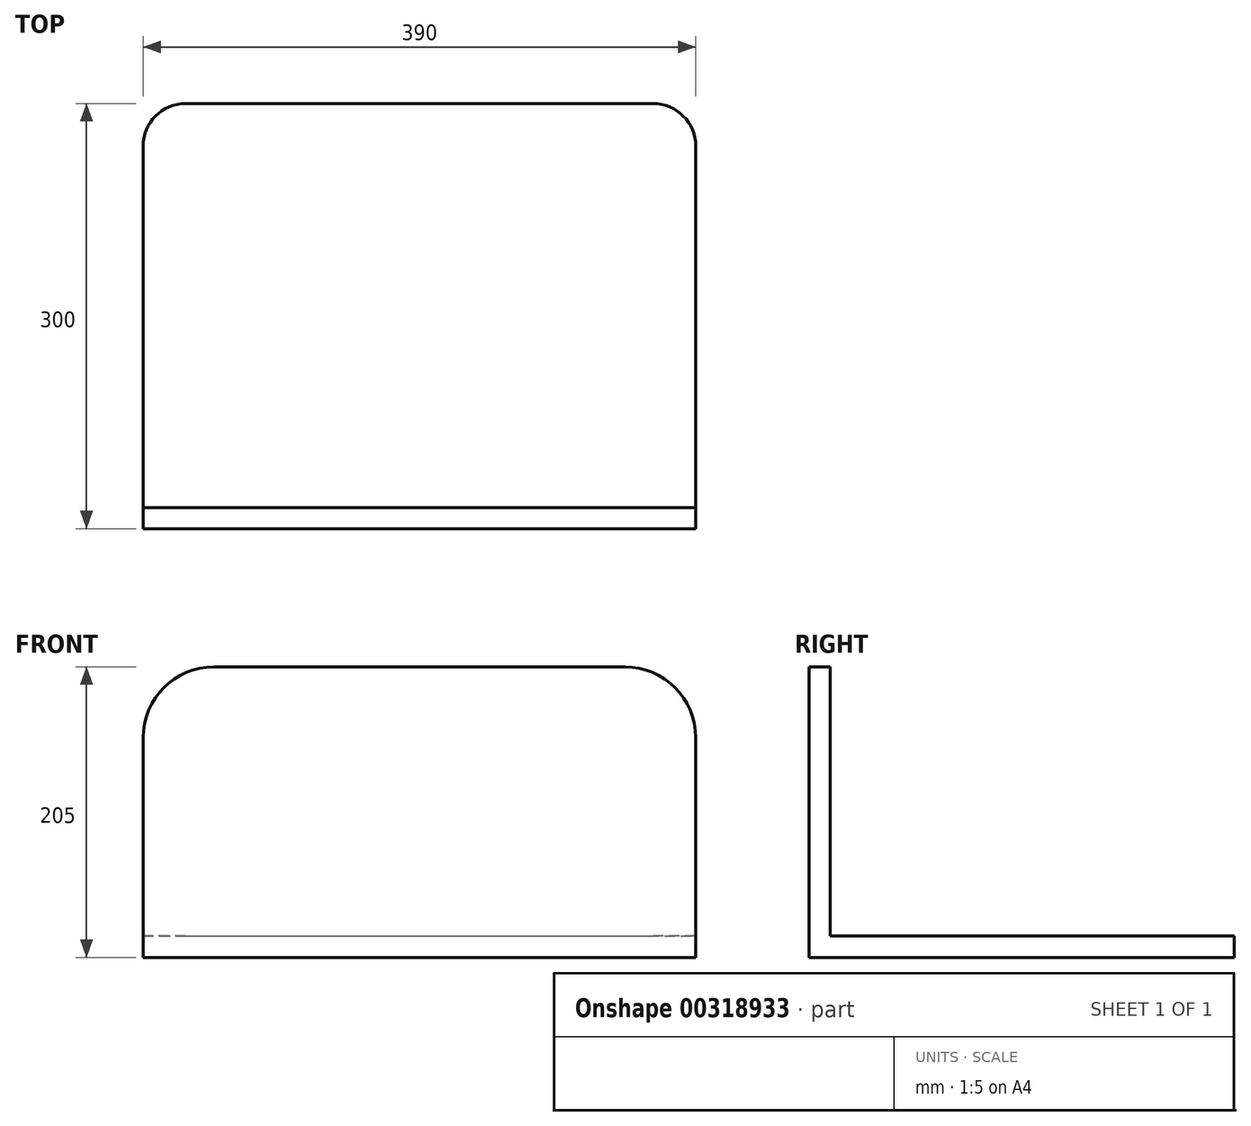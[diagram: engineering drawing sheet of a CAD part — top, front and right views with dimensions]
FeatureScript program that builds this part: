
annotation { "Feature Type Name" : "Feature", "Feature Type Description" : "" }
export const myFeature = defineFeature(function(context is Context, id is Id, definition is map)
    precondition{}
    {
        {
            var Q0;
            Q0=qCreatedBy(makeId("Top.planeOp"),FACE);
            var sketch = newSketch(context, id + "F0", { "sketchPlane" : qUnion([Q0])});
            skLineSegment(sketch, "E0.bottom", {"start": v(-195, -150) * mm, "end": v(195, -150) * mm});
            skLineSegment(sketch, "E0.top", {"start": v(-165, 150) * mm, "end": v(165, 150) * mm});
            skLineSegment(sketch, "E0.left", {"start": v(-195, -150) * mm, "end": v(-195, 120) * mm});
            skLineSegment(sketch, "E0.right", {"start": v(195, -150) * mm, "end": v(195, 120) * mm});
            skPoint(sketch, "E1.visualSharp", {"position": v(-195, 150) * mm});
            skArc(sketch, "E1.filletArc", {"start": v(-165, 150) * mm, "mid": v(-186.21, 141.21) * mm, "end": v(-195, 120) * mm});
            skPoint(sketch, "E2.visualSharp", {"position": v(195, 150) * mm});
            skArc(sketch, "E2.filletArc", {"start": v(195, 120) * mm, "mid": v(186.21, 141.21) * mm, "end": v(165, 150) * mm});
            skSolve(sketch);
        }
        {
            var Q0;
            Q0 = qSketchRegion(id + "F0", true);
            extrude(context, id + "F1", {"entities" : qUnion([Q0]), "depth" : 15 * mm, "offsetDistance" : 25 * mm});
        }
        {
            var Q0;
            Q0=makeQuery(id+"F1.opExtrude","CAP_FACE",FACE,{"disambiguationData":[OSD([sQuery(id+"F0.wireOp",EDGE,"E0.bottom"),sQuery(id+"F0.wireOp",EDGE,"E0.top"),sQuery(id+"F0.wireOp",EDGE,"E0.left"),sQuery(id+"F0.wireOp",EDGE,"E0.right"),sQuery(id+"F0.wireOp",EDGE,"E1.filletArc"),sQuery(id+"F0.wireOp",EDGE,"E2.filletArc")])],"isStart":false});
            var sketch = newSketch(context, id + "F2", { "sketchPlane" : qUnion([Q0])});
            skLineSegment(sketch, "E3.bottom", {"start": v(-195, -150) * mm, "end": v(195, -150) * mm});
            skLineSegment(sketch, "E3.top", {"start": v(-195, -135) * mm, "end": v(195, -135) * mm});
            skLineSegment(sketch, "E3.left", {"start": v(-195, -150) * mm, "end": v(-195, -135) * mm});
            skLineSegment(sketch, "E3.right", {"start": v(195, -150) * mm, "end": v(195, -135) * mm});
            skSolve(sketch);
        }
        {
            var Q0;
            Q0=makeQuery(id+"F2.imprint","IMPRINT",FACE,{"disambiguationData":[TD([[makeQuery(id+"F2.imprint","IMPRINT",EDGE,{"derivedFrom":sQuery(id+"F2.wireOp",EDGE,"E3.bottom")}),1.0]])]});
            extrude(context, id + "F3", {"entities" : qUnion([Q0]), "operationType" : NewBodyOperationType.ADD, "depth" : 190 * mm, "offsetDistance" : 25 * mm});
        }
        {
            var Q0;
            Q0=makeQuery(id+"F3.opExtrude","CAP_EDGE",EDGE,{"disambiguationData":[OSD([sQuery(id+"F2.wireOp",EDGE,"E3.right")])],"isStart":false});
            var Q1;
            Q1=makeQuery(id+"F3.opExtrude","CAP_EDGE",EDGE,{"disambiguationData":[OSD([sQuery(id+"F2.wireOp",EDGE,"E3.left")])],"isStart":false});
            fillet(context, id + "F4", {"entities" : qUnion([Q0, Q1]), "radius" : 50 * mm, "tangentPropagation" : true, "allowEdgeOverflow" : false});
        }
    });
